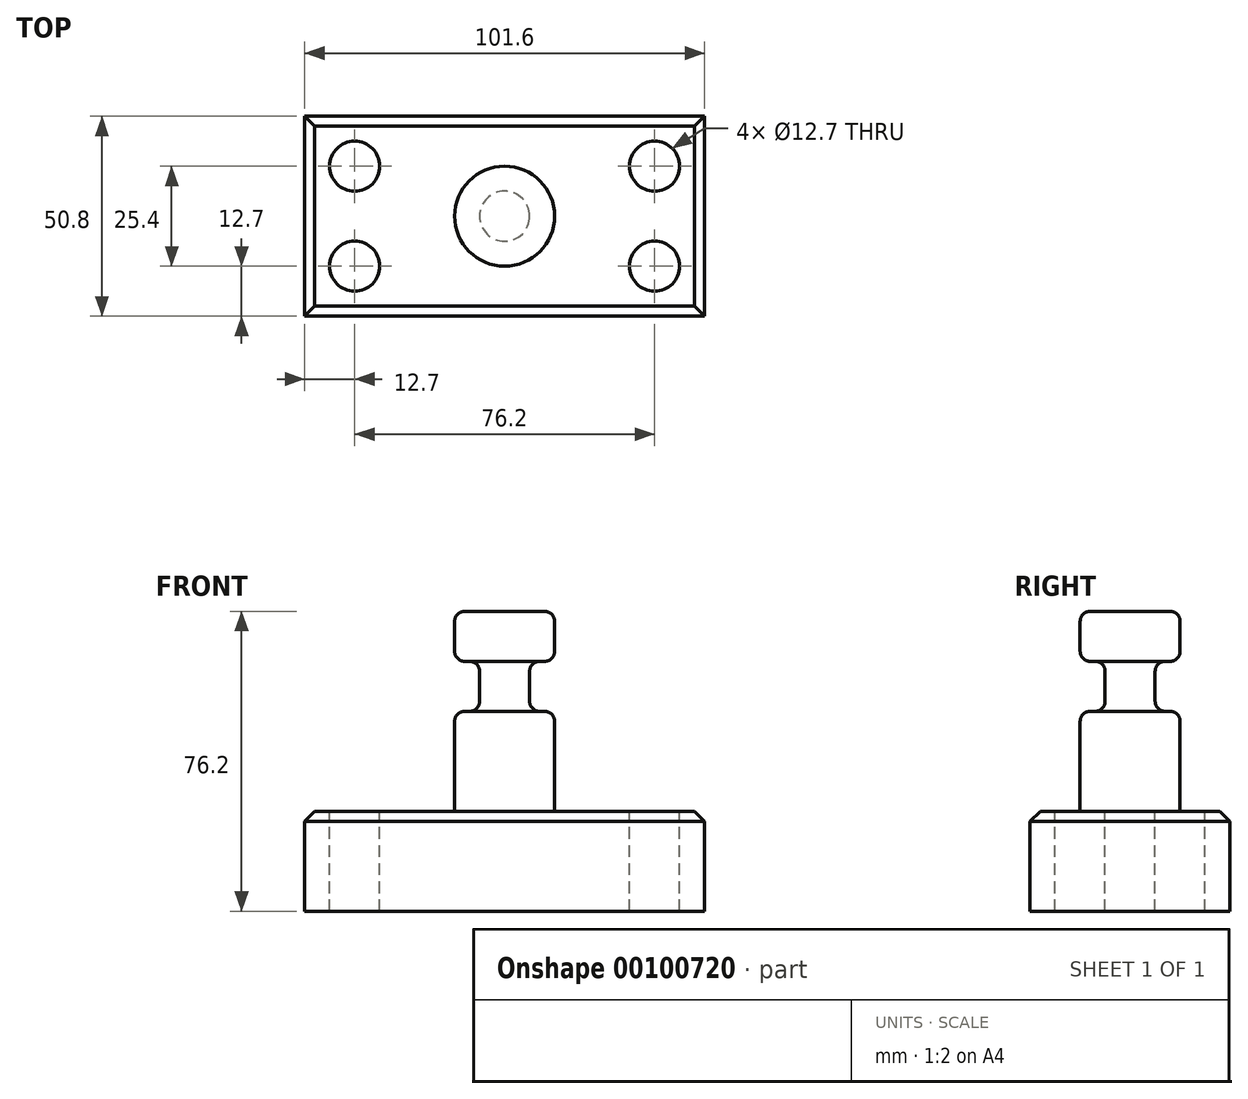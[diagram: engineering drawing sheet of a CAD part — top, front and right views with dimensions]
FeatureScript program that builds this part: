
annotation { "Feature Type Name" : "Feature", "Feature Type Description" : "" }
export const myFeature = defineFeature(function(context is Context, id is Id, definition is map)
    precondition{}
    {
        {
            var Q0;
            Q0=qCreatedBy(makeId("Top.planeOp"),FACE);
            var sketch = newSketch(context, id + "F0", { "sketchPlane" : qUnion([Q0])});
            skLineSegment(sketch, "E0.bottom", {"start": v(50.8, -25.4) * mm, "end": v(-50.8, -25.4) * mm});
            skLineSegment(sketch, "E0.top", {"start": v(50.8, 25.4) * mm, "end": v(-50.8, 25.4) * mm});
            skLineSegment(sketch, "E0.left", {"start": v(50.8, -25.4) * mm, "end": v(50.8, 25.4) * mm});
            skLineSegment(sketch, "E0.right", {"start": v(-50.8, -25.4) * mm, "end": v(-50.8, 25.4) * mm});
            skPoint(sketch, "E0.middle", {"position": v(0, 0) * mm});
            skSolve(sketch);
        }
        {
            var Q0;
            Q0=makeQuery(id+"F0.imprint","IMPRINT",FACE,{"disambiguationData":[TD([[makeQuery(id+"F0.imprint","IMPRINT",EDGE,{"derivedFrom":sQuery(id+"F0.wireOp",EDGE,"E0.bottom")}),-1.0]])]});
            extrude(context, id + "F1", {"entities" : qUnion([Q0]), "depth" : 25.4 * mm});
        }
        {
            var Q0;
            Q0=makeQuery(id+"F1.opExtrude","CAP_FACE",FACE,{"disambiguationData":[OSD([sQuery(id+"F0.wireOp",EDGE,"E0.bottom"),sQuery(id+"F0.wireOp",EDGE,"E0.top"),sQuery(id+"F0.wireOp",EDGE,"E0.left"),sQuery(id+"F0.wireOp",EDGE,"E0.right")])],"isStart":false});
            var sketch = newSketch(context, id + "F2", { "sketchPlane" : qUnion([Q0])});
            skCircle(sketch, "E1", {"center": v(-38.1, 12.7) * mm, "radius": 6.35 * mm});
            skCircle(sketch, "E2", {"center": v(-38.1, -12.7) * mm, "radius": 6.35 * mm});
            skCircle(sketch, "E3", {"center": v(38.1, 12.7) * mm, "radius": 6.35 * mm});
            skCircle(sketch, "E4", {"center": v(38.1, -12.7) * mm, "radius": 6.35 * mm});
            skSolve(sketch);
        }
        {
            var Q0;
            Q0 = qSketchRegion(id + "F2", true);
            extrude(context, id + "F3", {"entities" : qUnion([Q0]), "operationType" : NewBodyOperationType.REMOVE, "endBound" : BoundingType.THROUGH_ALL, "oppositeDirection" : true, "depth" : 25.4 * mm});
        }
        {
            var Q0;
            Q0=qCreatedBy(makeId("Front.planeOp"),FACE);
            var sketch = newSketch(context, id + "F4", { "sketchPlane" : qUnion([Q0])});
            skLineSegment(sketch, "E5.bottom", {"start": v(0, 25.4) * mm, "end": v(-12.7, 25.4) * mm});
            skLineSegment(sketch, "E5.top", {"start": v(0, 76.2) * mm, "end": v(-12.7, 76.2) * mm});
            skLineSegment(sketch, "E5.left", {"start": v(0, 25.4) * mm, "end": v(0, 76.2) * mm});
            skLineSegment(sketch, "E5.right", {"start": v(-12.7, 25.4) * mm, "end": v(-12.7, 76.2) * mm});
            skSolve(sketch);
        }
        {
            var Q0;
            Q0 = qSketchRegion(id + "F4", true);
            var Q1;
            Q1=sQuery(id+"F4.wireOp",EDGE,"E5.left");
            revolve(context, id + "F5", {"operationType" : NewBodyOperationType.ADD, "entities" : qUnion([Q0]), "axis" : qUnion([Q1]), "revolveType" : RevolveType.FULL});
        }
        {
            var Q0;
            Q0=qCreatedBy(makeId("Front.planeOp"),FACE);
            var sketch = newSketch(context, id + "F6", { "sketchPlane" : qUnion([Q0])});
            skLineSegment(sketch, "E6.bottom", {"start": v(-20.43, 63.5) * mm, "end": v(-6.35, 63.5) * mm});
            skLineSegment(sketch, "E6.top", {"start": v(-20.43, 50.8) * mm, "end": v(-6.35, 50.8) * mm});
            skLineSegment(sketch, "E6.left", {"start": v(-20.43, 63.5) * mm, "end": v(-20.43, 50.8) * mm});
            skLineSegment(sketch, "E6.right", {"start": v(-6.35, 63.5) * mm, "end": v(-6.35, 50.8) * mm});
            skLineSegment(sketch, "E7", {"start": v(0, 0) * mm, "end": v(0, 78.14) * mm, "construction": true});
            skSolve(sketch);
        }
        {
            var Q0;
            Q0=makeQuery(id+"F6.imprint","IMPRINT",FACE,{"disambiguationData":[TD([[makeQuery(id+"F6.imprint","IMPRINT",EDGE,{"derivedFrom":sQuery(id+"F6.wireOp",EDGE,"E6.bottom")}),-1.0]])]});
            var Q1;
            Q1=sQuery(id+"F6.wireOp",EDGE,"E7");
            revolve(context, id + "F7", {"operationType" : NewBodyOperationType.REMOVE, "entities" : qUnion([Q0]), "axis" : qUnion([Q1]), "revolveType" : RevolveType.FULL, "oppositeDirection" : true});
        }
        {
            var Q0;
            Q0=makeQuery(id+"F7.boolean.opBoolean","INTERSECT",EDGE,{"derivedFrom":[makeQuery(id+"F5.opRevolve","SWEPT_FACE",FACE,{"disambiguationData":[OSD([sQuery(id+"F4.wireOp",EDGE,"E5.right")])]}),makeQuery(id+"F7.opRevolve","SWEPT_FACE",FACE,{"disambiguationData":[OSD([sQuery(id+"F6.wireOp",EDGE,"E6.top")])]})]});
            var Q1;
            Q1=makeQuery(id+"F7.boolean.opBoolean","COPY",EDGE,{"derivedFrom":makeQuery(id+"F7.opRevolve","SWEPT_EDGE",EDGE,{"disambiguationData":[OSD([sQuery(id+"F6.wireOp",EDGE,"E6.top"),sQuery(id+"F6.wireOp",EDGE,"E6.right")])]})});
            var Q2;
            Q2=makeQuery(id+"F5.opRevolve","SWEPT_EDGE",EDGE,{"disambiguationData":[OSD([sQuery(id+"F4.wireOp",EDGE,"E5.top"),sQuery(id+"F4.wireOp",EDGE,"E5.right")])]});
            var Q3;
            Q3=makeQuery(id+"F7.boolean.opBoolean","INTERSECT",EDGE,{"derivedFrom":[makeQuery(id+"F5.opRevolve","SWEPT_FACE",FACE,{"disambiguationData":[OSD([sQuery(id+"F4.wireOp",EDGE,"E5.right")])]}),makeQuery(id+"F7.opRevolve","SWEPT_FACE",FACE,{"disambiguationData":[OSD([sQuery(id+"F6.wireOp",EDGE,"E6.bottom")])]})]});
            var Q4;
            Q4=makeQuery(id+"F7.boolean.opBoolean","COPY",EDGE,{"derivedFrom":makeQuery(id+"F7.opRevolve","SWEPT_EDGE",EDGE,{"disambiguationData":[OSD([sQuery(id+"F6.wireOp",EDGE,"E6.bottom"),sQuery(id+"F6.wireOp",EDGE,"E6.right")])]})});
            var Q5;
            Q5=makeQuery(id+"F5.opRevolve","SWEPT_EDGE",EDGE,{"disambiguationData":[OSD([sQuery(id+"F4.wireOp",EDGE,"E5.bottom"),sQuery(id+"F4.wireOp",EDGE,"E5.right")])]});
            fillet(context, id + "F8", {"entities" : qUnion([Q0, Q1, Q2, Q3, Q4, Q5]), "radius" : 2.54 * mm, "tangentPropagation" : true, "allowEdgeOverflow" : false});
        }
        {
            var Q0;
            Q0=makeQuery(id+"F1.opExtrude","CAP_EDGE",EDGE,{"disambiguationData":[OSD([sQuery(id+"F0.wireOp",EDGE,"E0.bottom")])],"isStart":false});
            var Q1;
            Q1=makeQuery(id+"F1.opExtrude","CAP_EDGE",EDGE,{"disambiguationData":[OSD([sQuery(id+"F0.wireOp",EDGE,"E0.right")])],"isStart":false});
            var Q2;
            Q2=makeQuery(id+"F1.opExtrude","CAP_EDGE",EDGE,{"disambiguationData":[OSD([sQuery(id+"F0.wireOp",EDGE,"E0.top")])],"isStart":false});
            var Q3;
            Q3=makeQuery(id+"F1.opExtrude","CAP_EDGE",EDGE,{"disambiguationData":[OSD([sQuery(id+"F0.wireOp",EDGE,"E0.left")])],"isStart":false});
            chamfer(context, id + "F9", {"entities" : qUnion([Q0, Q1, Q2, Q3]), "width" : 2.54 * mm, "tangentPropagation" : true});
        }
    });
